# Revit family: Plymold-Aurora-Table_Dining_Counter
name_source: partatom
category: Furniture
units: mm (PartAtom-declared; Revit-internal decimal feet)

## family parameters
Always vertical = Yes
Cut with Voids When Loaded = No
OmniClass Number = 23.40.20.00
OmniClass Title = General Furniture and Specialties
Render Appearance Source = Family Geometry
Room Calculation Point = No
Shared = No
Work Plane-Based = No

## types (4) — shared parameters
Assembly Code = E2020200
Default Elevation = 0"
Depth = 19"
FRAME MATERIAL = PLY - Onyx Black Powdercoat
FootRest = Yes
GLIDE MATERIAL = PLY - Plastic Black
HARDWARE MATERIAL = PLY - Onyx Black Powdercoat
Keynote = 12500
MODESTY PANEL MATERIAL = PLY - Wood Mahogany
Manufacturer = Plymold Inc.
POWER FINISH = PLY - Plastic Black
Product Documentation Link = https://plymold.com
Revit Model Built By = https://servex-us.com
Sustainability = https://plymold.com
TOP EDGE MATERIAL = PLY - Plastic Black
TOP MATERIAL = PLY - Wood Mahogany
Type Comments = Dining Counter
URL = https://plymold.com

## per-type parameters (varying)
| type | Description | FR Height | Height | Width |
| 1904830 | Powered Dining Counter - 48" Dining Height ADA | 5 7/8" | 30" | 48" |
| 1909642 | Powered Dining Counter - 96" Long Bar Height | 11 7/8" | 42" | 96" |
| 1904842 | Powered Dining Counter - 48" Long Bar Height | 11 7/8" | 42" | 48" |
| 1907242 | Powered Dining Counter - 72" Long Bar Height | 11 7/8" | 42" | 72" |

note: column(s) folded — value = type name in every type: Model

## geometry (parser evidence)
native form markers: Sweep x5
no freeform markers — native parametric forms only
